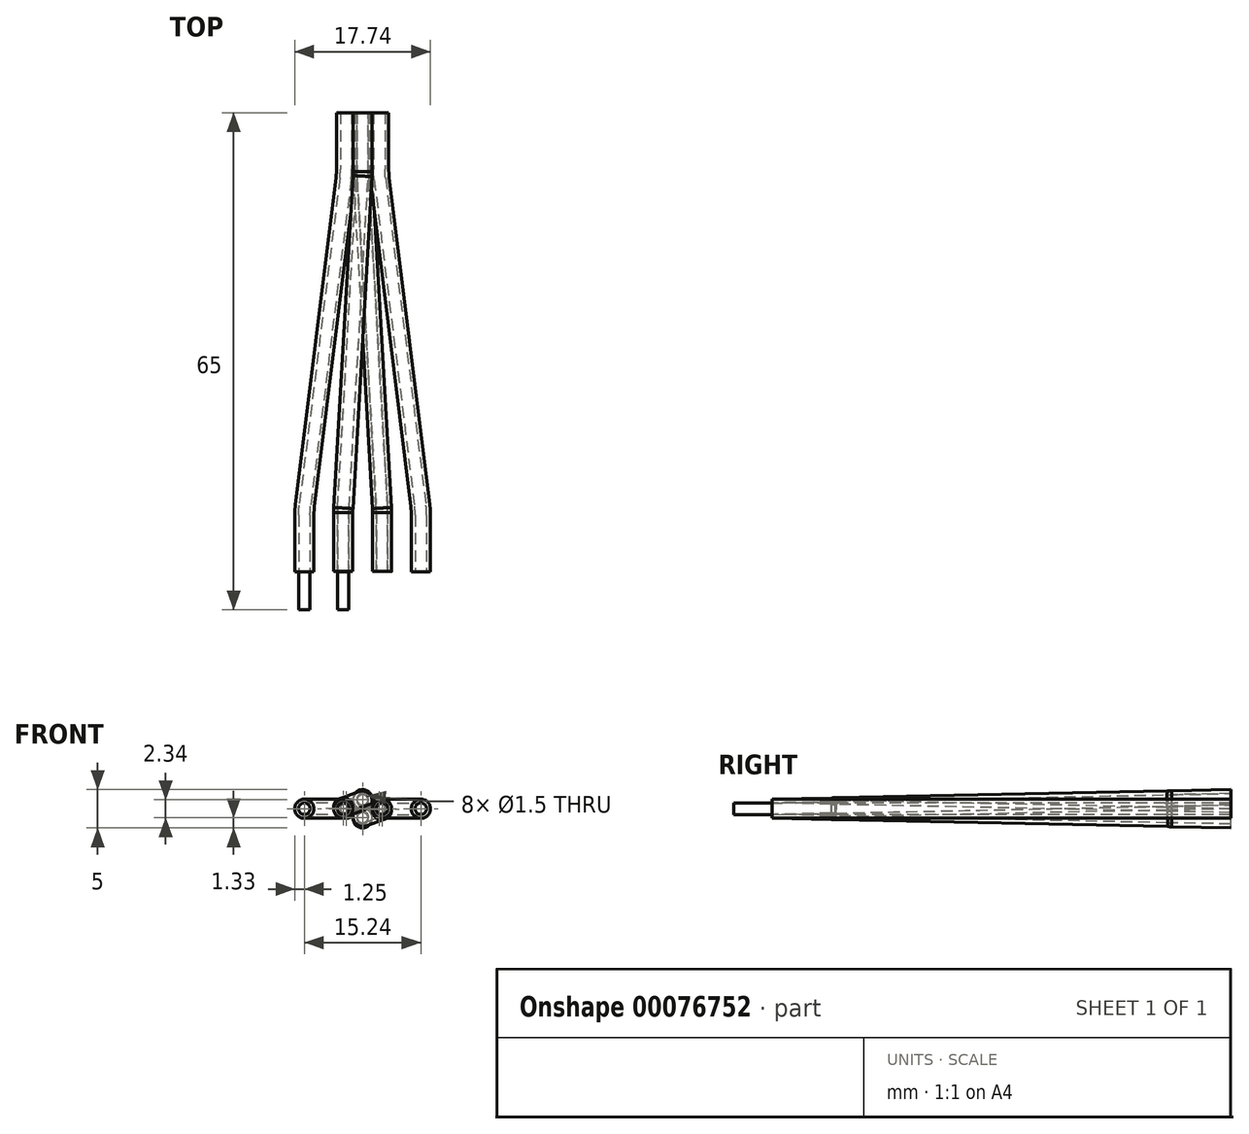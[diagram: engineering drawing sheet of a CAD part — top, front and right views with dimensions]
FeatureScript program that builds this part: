
annotation { "Feature Type Name" : "Feature", "Feature Type Description" : "" }
export const myFeature = defineFeature(function(context is Context, id is Id, definition is map)
    precondition{}
    {
        {
            var Q0;
            Q0=qCreatedBy(makeId("Front.planeOp"),FACE);
            var sketch = newSketch(context, id + "F0", { "sketchPlane" : qUnion([Q0])});
            skCircle(sketch, "E0", {"center": v(0, 1.25) * mm, "radius": 1.25 * mm});
            skCircle(sketch, "E1", {"center": v(0, 1.25) * mm, "radius": 0.75 * mm});
            skCircle(sketch, "E2.MirrorC", {"center": v(0, -1.25) * mm, "radius": 1.25 * mm});
            skCircle(sketch, "E3.MirrorC", {"center": v(0, -1.25) * mm, "radius": 0.75 * mm});
            skCircle(sketch, "E4", {"center": v(2.17, 0) * mm, "radius": 1.25 * mm});
            skCircle(sketch, "E5", {"center": v(2.17, 0) * mm, "radius": 0.75 * mm});
            skCircle(sketch, "E6.MirrorC", {"center": v(-2.17, 0) * mm, "radius": 1.25 * mm});
            skCircle(sketch, "E7.MirrorC", {"center": v(-2.17, 0) * mm, "radius": 0.75 * mm});
            skSolve(sketch);
        }
        {
            var Q0;
            Q0=qCreatedBy(makeId("Front.planeOp"),FACE);
            cPlane(context, id + "F1", {"entities" : qUnion([Q0]), "cplaneType" : CPlaneType.OFFSET, "offset" : 60 * mm, "width" : 150 * mm, "height" : 150 * mm});
        }
        {
            var Q0;
            Q0=qCreatedBy(id+"F1.planeOp",FACE);
            var sketch = newSketch(context, id + "F2", { "sketchPlane" : qUnion([Q0])});
            skCircle(sketch, "E8", {"center": v(-2.54, 0) * mm, "radius": 0.75 * mm});
            skCircle(sketch, "E9", {"center": v(-7.62, 0) * mm, "radius": 0.75 * mm});
            skCircle(sketch, "E10.MirrorC", {"center": v(2.54, 0) * mm, "radius": 0.75 * mm});
            skCircle(sketch, "E11.MirrorC", {"center": v(7.62, 0) * mm, "radius": 0.75 * mm});
            skSolve(sketch);
        }
        {
            var Q0;
            Q0=qCreatedBy(makeId("Top.planeOp"),FACE);
            var sketch = newSketch(context, id + "F3", { "sketchPlane" : qUnion([Q0])});
            skLineSegment(sketch, "E12", {"start": v(-7.62, -60) * mm, "end": v(-7.62, -52.62) * mm});
            skLineSegment(sketch, "E13", {"start": v(-7.54, -51.39) * mm, "end": v(-2.24, -8.61) * mm});
            skLineSegment(sketch, "E14", {"start": v(-2.17, -7.38) * mm, "end": v(-2.17, 0) * mm});
            skPoint(sketch, "E15.visualSharp", {"position": v(-7.62, -52) * mm});
            skArc(sketch, "E15.filletArc", {"start": v(-7.54, -51.39) * mm, "mid": v(-7.6, -52) * mm, "end": v(-7.62, -52.62) * mm});
            skPoint(sketch, "E16.visualSharp", {"position": v(-2.17, -8) * mm});
            skArc(sketch, "E16.filletArc", {"start": v(-2.24, -8.61) * mm, "mid": v(-2.18, -8) * mm, "end": v(-2.17, -7.38) * mm});
            skLineSegment(sketch, "E17.MirrorCS", {"start": v(7.62, -60) * mm, "end": v(7.62, -52.62) * mm});
            skPoint(sketch, "E18.MirrorP", {"position": v(2.17, -8) * mm});
            skArc(sketch, "E19.MirrorCS", {"start": v(7.54, -51.39) * mm, "mid": v(7.6, -52) * mm, "end": v(7.62, -52.62) * mm});
            skLineSegment(sketch, "E20.MirrorCS", {"start": v(2.17, -7.38) * mm, "end": v(2.17, 0) * mm});
            skLineSegment(sketch, "E21.MirrorCS", {"start": v(7.54, -51.39) * mm, "end": v(2.24, -8.61) * mm});
            skArc(sketch, "E22.MirrorCS", {"start": v(2.24, -8.61) * mm, "mid": v(2.18, -8) * mm, "end": v(2.17, -7.38) * mm});
            skPoint(sketch, "E23.MirrorP", {"position": v(7.62, -52) * mm});
            skSolve(sketch);
        }
        {
            var Q0;
            Q0=sQuery(id+"F2.wireOp",VERTEX,"E10.MirrorC.center");
            var Q1;
            Q1=sQuery(id+"F2.wireOp",VERTEX,"E8.center");
            var Q2;
            Q2=sQuery(id+"F0.wireOp",VERTEX,"E3.MirrorC.center");
            cPlane(context, id + "F4", {"entities" : qUnion([Q0, Q1, Q2]), "cplaneType" : CPlaneType.THREE_POINT, "offset" : 25 * mm, "width" : 150 * mm, "height" : 150 * mm});
        }
        {
            var Q0;
            Q0=qCreatedBy(id+"F4.planeOp",FACE);
            var sketch = newSketch(context, id + "F5", { "sketchPlane" : qUnion([Q0])});
            skLineSegment(sketch, "E24", {"start": v(2.54, -59.99) * mm, "end": v(2.54, -52.28) * mm});
            skLineSegment(sketch, "E25", {"start": v(2.52, -51.7) * mm, "end": v(0.02, -8.29) * mm});
            skLineSegment(sketch, "E26", {"start": v(0, -7.71) * mm, "end": v(0, 0) * mm});
            skPoint(sketch, "E27.visualSharp", {"position": v(2.54, -51.99) * mm});
            skArc(sketch, "E27.filletArc", {"start": v(2.54, -52.28) * mm, "mid": v(2.54, -51.99) * mm, "end": v(2.52, -51.7) * mm});
            skPoint(sketch, "E28.visualSharp", {"position": v(0, -8) * mm});
            skArc(sketch, "E28.filletArc", {"start": v(0, -7.71) * mm, "mid": v(0, -8) * mm, "end": v(0.02, -8.29) * mm});
            skSolve(sketch);
        }
        {
            var Q0;
            Q0=sQuery(id+"F0.wireOp",VERTEX,"E0.center");
            var Q1;
            Q1=sQuery(id+"F2.wireOp",VERTEX,"E8.center");
            var Q2;
            Q2=sQuery(id+"F5.wireOp",VERTEX,"E24.start");
            cPlane(context, id + "F6", {"entities" : qUnion([Q0, Q1, Q2]), "cplaneType" : CPlaneType.THREE_POINT, "offset" : 25 * mm, "width" : 150 * mm, "height" : 150 * mm});
        }
        {
            var Q0;
            Q0=qCreatedBy(id+"F6.planeOp",FACE);
            var sketch = newSketch(context, id + "F7", { "sketchPlane" : qUnion([Q0])});
            skLineSegment(sketch, "E29", {"start": v(0, 0) * mm, "end": v(0, 7.71) * mm});
            skLineSegment(sketch, "E30", {"start": v(-0.02, 8.29) * mm, "end": v(-2.52, 51.7) * mm});
            skLineSegment(sketch, "E31", {"start": v(-2.54, 52.28) * mm, "end": v(-2.54, 59.99) * mm});
            skPoint(sketch, "E32.visualSharp", {"position": v(-2.54, 51.99) * mm});
            skArc(sketch, "E32.filletArc", {"start": v(-2.54, 52.28) * mm, "mid": v(-2.54, 51.99) * mm, "end": v(-2.52, 51.7) * mm});
            skPoint(sketch, "E33.visualSharp", {"position": v(0, 8) * mm});
            skArc(sketch, "E33.filletArc", {"start": v(0, 7.71) * mm, "mid": v(0, 8) * mm, "end": v(-0.02, 8.29) * mm});
            skSolve(sketch);
        }
        {
            var Q0;
            Q0=makeQuery(id+"F0.imprint","IMPRINT",FACE,{"disambiguationData":[TD([[makeQuery(id+"F0.imprint","IMPRINT",EDGE,{"derivedFrom":sQuery(id+"F0.wireOp",EDGE,"E1")}),1.0]])]});
            var Q1;
            Q1=sQuery(id+"F7.wireOp",EDGE,"E31");
            var Q2;
            Q2=sQuery(id+"F7.wireOp",EDGE,"E32.filletArc");
            var Q3;
            Q3=sQuery(id+"F7.wireOp",EDGE,"E30");
            var Q4;
            Q4=sQuery(id+"F7.wireOp",EDGE,"E33.filletArc");
            var Q5;
            Q5=sQuery(id+"F7.wireOp",EDGE,"E29");
            sweep(context, id + "F8", {"profiles" : qUnion([Q0]), "path" : qUnion([Q1, Q2, Q3, Q4, Q5]), "keepProfileOrientation" : true});
        }
        {
            var Q0;
            Q0=makeQuery(id+"F0.imprint","IMPRINT",FACE,{"disambiguationData":[TD([[makeQuery(id+"F0.imprint","IMPRINT",EDGE,{"derivedFrom":sQuery(id+"F0.wireOp",EDGE,"E7.MirrorC")}),-1.0]])]});
            var Q1;
            Q1=sQuery(id+"F3.wireOp",EDGE,"E14");
            var Q2;
            Q2=sQuery(id+"F3.wireOp",EDGE,"E16.filletArc");
            var Q3;
            Q3=sQuery(id+"F3.wireOp",EDGE,"E13");
            var Q4;
            Q4=sQuery(id+"F3.wireOp",EDGE,"E15.filletArc");
            var Q5;
            Q5=sQuery(id+"F3.wireOp",EDGE,"E12");
            sweep(context, id + "F9", {"profiles" : qUnion([Q0]), "path" : qUnion([Q1, Q2, Q3, Q4, Q5])});
        }
        {
            var Q0;
            Q0=makeQuery(id+"F0.imprint","IMPRINT",FACE,{"disambiguationData":[TD([[makeQuery(id+"F0.imprint","IMPRINT",EDGE,{"derivedFrom":sQuery(id+"F0.wireOp",EDGE,"E3.MirrorC")}),-1.0]])]});
            var Q1;
            Q1=sQuery(id+"F5.wireOp",EDGE,"E26");
            var Q2;
            Q2=sQuery(id+"F5.wireOp",EDGE,"E28.filletArc");
            var Q3;
            Q3=sQuery(id+"F5.wireOp",EDGE,"E25");
            var Q4;
            Q4=sQuery(id+"F5.wireOp",EDGE,"E27.filletArc");
            var Q5;
            Q5=sQuery(id+"F5.wireOp",EDGE,"E24");
            sweep(context, id + "F10", {"profiles" : qUnion([Q0]), "path" : qUnion([Q1, Q2, Q3, Q4, Q5])});
        }
        {
            var Q0;
            Q0=makeQuery(id+"F0.imprint","IMPRINT",FACE,{"disambiguationData":[TD([[makeQuery(id+"F0.imprint","IMPRINT",EDGE,{"derivedFrom":sQuery(id+"F0.wireOp",EDGE,"E5")}),1.0]])]});
            var Q1;
            Q1=sQuery(id+"F3.wireOp",EDGE,"E20.MirrorCS");
            var Q2;
            Q2=sQuery(id+"F3.wireOp",EDGE,"E22.MirrorCS");
            var Q3;
            Q3=sQuery(id+"F3.wireOp",EDGE,"E21.MirrorCS");
            var Q4;
            Q4=sQuery(id+"F3.wireOp",EDGE,"E19.MirrorCS");
            var Q5;
            Q5=sQuery(id+"F3.wireOp",EDGE,"E17.MirrorCS");
            sweep(context, id + "F11", {"profiles" : qUnion([Q0]), "path" : qUnion([Q1, Q2, Q3, Q4, Q5])});
        }
        {
            var Q0;
            Q0=makeQuery(id+"F0.imprint","IMPRINT",FACE,{"disambiguationData":[TD([[makeQuery(id+"F0.imprint","IMPRINT",EDGE,{"derivedFrom":sQuery(id+"F0.wireOp",EDGE,"E5")}),-1.0]])]});
            var Q1;
            Q1=sQuery(id+"F3.wireOp",EDGE,"E20.MirrorCS");
            var Q2;
            Q2=sQuery(id+"F3.wireOp",EDGE,"E22.MirrorCS");
            var Q3;
            Q3=sQuery(id+"F3.wireOp",EDGE,"E21.MirrorCS");
            var Q4;
            Q4=sQuery(id+"F3.wireOp",EDGE,"E19.MirrorCS");
            var Q5;
            Q5=sQuery(id+"F3.wireOp",EDGE,"E17.MirrorCS");
            sweep(context, id + "F12", {"profiles" : qUnion([Q0]), "path" : qUnion([Q1, Q2, Q3, Q4, Q5])});
        }
        {
            var Q0;
            Q0=makeQuery(id+"F2.imprint","IMPRINT",FACE,{"disambiguationData":[TD([[makeQuery(id+"F2.imprint","IMPRINT",EDGE,{"derivedFrom":sQuery(id+"F2.wireOp",EDGE,"E11.MirrorC")}),-1.0]])]});
            var Q1;
            Q1=makeQuery(id+"F2.imprint","IMPRINT",FACE,{"disambiguationData":[TD([[makeQuery(id+"F2.imprint","IMPRINT",EDGE,{"derivedFrom":sQuery(id+"F2.wireOp",EDGE,"E10.MirrorC")}),-1.0]])]});
            var Q2;
            Q2=makeQuery(id+"F2.imprint","IMPRINT",FACE,{"disambiguationData":[TD([[makeQuery(id+"F2.imprint","IMPRINT",EDGE,{"derivedFrom":sQuery(id+"F2.wireOp",EDGE,"E8")}),1.0]])]});
            var Q3;
            Q3=makeQuery(id+"F2.imprint","IMPRINT",FACE,{"disambiguationData":[TD([[makeQuery(id+"F2.imprint","IMPRINT",EDGE,{"derivedFrom":sQuery(id+"F2.wireOp",EDGE,"E9")}),1.0]])]});
            var Q4;
            Q4=sQuery(id+"F2.wireOp",EDGE,"E11.MirrorC");
            extrude(context, id + "F13", {"entities" : qUnion([Q0, Q1, Q2, Q3]), "operationType" : NewBodyOperationType.ADD, "surfaceEntities" : qUnion([Q4]), "depth" : 5 * mm});
        }
        {
            var Q0;
            Q0=makeQuery(id+"F0.imprint","IMPRINT",FACE,{"disambiguationData":[TD([[makeQuery(id+"F0.imprint","IMPRINT",EDGE,{"derivedFrom":sQuery(id+"F0.wireOp",EDGE,"E7.MirrorC")}),1.0]])]});
            var Q1;
            Q1=sQuery(id+"F3.wireOp",EDGE,"E14");
            var Q2;
            Q2=sQuery(id+"F3.wireOp",EDGE,"E16.filletArc");
            var Q3;
            Q3=sQuery(id+"F3.wireOp",EDGE,"E13");
            var Q4;
            Q4=sQuery(id+"F3.wireOp",EDGE,"E15.filletArc");
            var Q5;
            Q5=sQuery(id+"F3.wireOp",EDGE,"E12");
            sweep(context, id + "F14", {"profiles" : qUnion([Q0]), "path" : qUnion([Q1, Q2, Q3, Q4, Q5])});
        }
        {
            var Q0;
            Q0=makeQuery(id+"F0.imprint","IMPRINT",FACE,{"disambiguationData":[TD([[makeQuery(id+"F0.imprint","IMPRINT",EDGE,{"derivedFrom":sQuery(id+"F0.wireOp",EDGE,"E3.MirrorC")}),1.0]])]});
            var Q1;
            Q1=sQuery(id+"F5.wireOp",EDGE,"E26");
            var Q2;
            Q2=sQuery(id+"F5.wireOp",EDGE,"E28.filletArc");
            var Q3;
            Q3=sQuery(id+"F5.wireOp",EDGE,"E25");
            var Q4;
            Q4=sQuery(id+"F5.wireOp",EDGE,"E24");
            var Q5;
            Q5=sQuery(id+"F5.wireOp",EDGE,"E27.filletArc");
            sweep(context, id + "F15", {"profiles" : qUnion([Q0]), "path" : qUnion([Q1, Q2, Q3, Q4, Q5])});
        }
        {
            var Q0;
            Q0=makeQuery(id+"F0.imprint","IMPRINT",FACE,{"disambiguationData":[TD([[makeQuery(id+"F0.imprint","IMPRINT",EDGE,{"derivedFrom":sQuery(id+"F0.wireOp",EDGE,"E1")}),-1.0]])]});
            var Q1;
            Q1=sQuery(id+"F7.wireOp",EDGE,"E29");
            var Q2;
            Q2=sQuery(id+"F7.wireOp",EDGE,"E33.filletArc");
            var Q3;
            Q3=sQuery(id+"F7.wireOp",EDGE,"E30");
            var Q4;
            Q4=sQuery(id+"F7.wireOp",EDGE,"E32.filletArc");
            var Q5;
            Q5=sQuery(id+"F7.wireOp",EDGE,"E31");
            sweep(context, id + "F16", {"profiles" : qUnion([Q0]), "path" : qUnion([Q1, Q2, Q3, Q4, Q5])});
        }
    });
